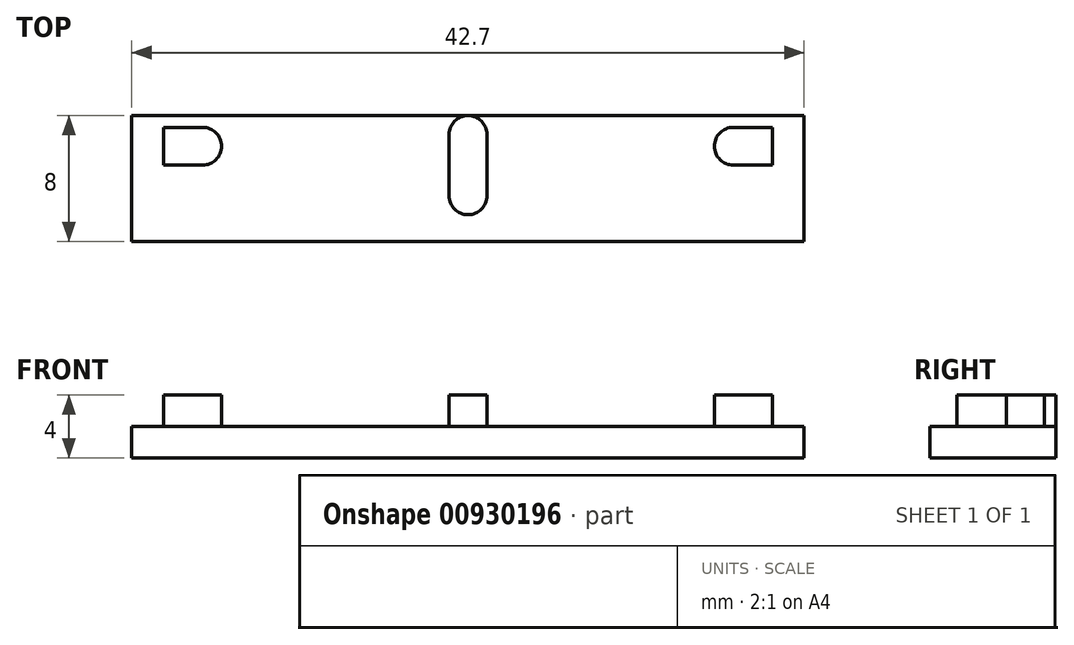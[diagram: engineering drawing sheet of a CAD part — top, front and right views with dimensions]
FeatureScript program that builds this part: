
annotation { "Feature Type Name" : "Feature", "Feature Type Description" : "" }
export const myFeature = defineFeature(function(context is Context, id is Id, definition is map)
    precondition{}
    {
        {
            var Q0;
            Q0=qCreatedBy(makeId("Top.planeOp"),FACE);
            var sketch = newSketch(context, id + "F0", { "sketchPlane" : qUnion([Q0])});
            skLineSegment(sketch, "E0.bottom", {"start": v(-19.35, 0) * mm, "end": v(19.35, 0) * mm});
            skLineSegment(sketch, "E0.top", {"start": v(-19.35, -12.3) * mm, "end": v(19.35, -12.3) * mm});
            skLineSegment(sketch, "E0.left", {"start": v(-19.35, 0) * mm, "end": v(-19.35, -1.15) * mm});
            skLineSegment(sketch, "E0.right", {"start": v(19.35, 0) * mm, "end": v(19.35, -1.15) * mm});
            skLineSegment(sketch, "E1.bottom", {"start": v(-19.85, 7) * mm, "end": v(19.85, 7) * mm});
            skLineSegment(sketch, "E1.top", {"start": v(-19.85, 0) * mm, "end": v(19.85, 0) * mm});
            skLineSegment(sketch, "E1.left", {"start": v(-19.85, 7) * mm, "end": v(-19.85, 0) * mm});
            skLineSegment(sketch, "E1.right", {"start": v(19.85, 7) * mm, "end": v(19.85, 0) * mm});
            skLineSegment(sketch, "E2", {"start": v(-19.35, -1.15) * mm, "end": v(-16.85, -1.15) * mm});
            skLineSegment(sketch, "E3", {"start": v(-19.35, -3.55) * mm, "end": v(-16.85, -3.55) * mm});
            skLineSegment(sketch, "E4", {"start": v(16.85, -3.55) * mm, "end": v(19.35, -3.55) * mm});
            skLineSegment(sketch, "E5", {"start": v(16.85, -1.15) * mm, "end": v(19.35, -1.15) * mm});
            skLineSegment(sketch, "E6.trimOffspring", {"start": v(-19.35, -3.55) * mm, "end": v(-19.35, -12.3) * mm});
            skLineSegment(sketch, "E7.trimOffspring", {"start": v(19.35, -3.55) * mm, "end": v(19.35, -12.3) * mm});
            skArc(sketch, "E8", {"start": v(-16.85, -3.55) * mm, "mid": v(-15.65, -2.35) * mm, "end": v(-16.85, -1.15) * mm});
            skArc(sketch, "E9", {"start": v(16.85, -1.15) * mm, "mid": v(15.65, -2.35) * mm, "end": v(16.85, -3.55) * mm});
            skLineSegment(sketch, "E10", {"start": v(-16.85, -2.35) * mm, "end": v(-15.65, -2.35) * mm, "construction": true});
            skLineSegment(sketch, "E11", {"start": v(-15.65, -2.35) * mm, "end": v(15.65, -2.35) * mm, "construction": true});
            skLineSegment(sketch, "E12", {"start": v(15.65, -2.35) * mm, "end": v(16.85, -2.35) * mm, "construction": true});
            skLineSegment(sketch, "E13", {"start": v(-1.2, -5.5) * mm, "end": v(-1.2, -1.6) * mm});
            skLineSegment(sketch, "E14", {"start": v(1.2, -5.5) * mm, "end": v(1.2, -1.6) * mm});
            skArc(sketch, "E15", {"start": v(1.2, -1.6) * mm, "mid": v(0, -0.4) * mm, "end": v(-1.2, -1.6) * mm});
            skArc(sketch, "E16", {"start": v(-1.2, -5.5) * mm, "mid": v(0, -6.7) * mm, "end": v(1.2, -5.5) * mm});
            skLineSegment(sketch, "E17", {"start": v(0, -1.6) * mm, "end": v(0, -5.5) * mm, "construction": true});
            skLineSegment(sketch, "E18", {"start": v(0, -1.6) * mm, "end": v(0, 0) * mm, "construction": true});
            skLineSegment(sketch, "E19", {"start": v(0, -0.4) * mm, "end": v(0, -6.7) * mm, "construction": true});
            skLineSegment(sketch, "E20", {"start": v(-19.35, -1.15) * mm, "end": v(-19.35, -3.55) * mm});
            skLineSegment(sketch, "E21", {"start": v(19.35, -1.15) * mm, "end": v(19.35, -3.55) * mm});
            skSolve(sketch);
        }
        {
            var Q0;
            Q0=makeQuery(id+"F0.imprint","IMPRINT",FACE,{"disambiguationData":[TD([[makeQuery(id+"F0.imprint","IMPRINT",EDGE,{"derivedFrom":sQuery(id+"F0.wireOp",EDGE,"E13")}),-1.0]])]});
            var Q1;
            Q1=makeQuery(id+"F0.imprint","IMPRINT",FACE,{"disambiguationData":[TD([[makeQuery(id+"F0.imprint","IMPRINT",EDGE,{"derivedFrom":sQuery(id+"F0.wireOp",EDGE,"E2")}),-1.0]])]});
            var Q2;
            Q2=makeQuery(id+"F0.imprint","IMPRINT",FACE,{"disambiguationData":[TD([[makeQuery(id+"F0.imprint","IMPRINT",EDGE,{"derivedFrom":sQuery(id+"F0.wireOp",EDGE,"E4")}),1.0]])]});
            extrude(context, id + "F1", {"entities" : qUnion([Q0, Q1, Q2]), "depth" : 2 * mm, "offsetDistance" : 25 * mm});
        }
        {
            var Q0;
            Q0=qCreatedBy(makeId("Top.planeOp"),FACE);
            var sketch = newSketch(context, id + "F2", { "sketchPlane" : qUnion([Q0])});
            skArc(sketch, "E22.0.0", {"start": v(-1.2, -5.5) * mm, "mid": v(0, -6.7) * mm, "end": v(1.2, -5.5) * mm, "construction": true});
            skLineSegment(sketch, "E22.0.1", {"start": v(1.2, -5.5) * mm, "end": v(1.2, -1.6) * mm, "construction": true});
            skArc(sketch, "E22.0.2", {"start": v(1.2, -1.6) * mm, "mid": v(0, -0.4) * mm, "end": v(-1.2, -1.6) * mm, "construction": true});
            skLineSegment(sketch, "E22.0.3", {"start": v(-1.2, -1.6) * mm, "end": v(-1.2, -5.5) * mm, "construction": true});
            skLineSegment(sketch, "E23.0.0", {"start": v(-19.35, -1.15) * mm, "end": v(-19.35, -3.55) * mm, "construction": true});
            skLineSegment(sketch, "E23.0.1", {"start": v(-19.35, -3.55) * mm, "end": v(-16.85, -3.55) * mm, "construction": true});
            skArc(sketch, "E23.0.2", {"start": v(-16.85, -3.55) * mm, "mid": v(-15.65, -2.35) * mm, "end": v(-16.85, -1.15) * mm, "construction": true});
            skLineSegment(sketch, "E23.0.3", {"start": v(-16.85, -1.15) * mm, "end": v(-19.35, -1.15) * mm, "construction": true});
            skLineSegment(sketch, "E24.bottom", {"start": v(21.35, -0.4) * mm, "end": v(-21.35, -0.4) * mm});
            skLineSegment(sketch, "E24.top", {"start": v(21.35, -8.4) * mm, "end": v(-21.35, -8.4) * mm});
            skLineSegment(sketch, "E24.left", {"start": v(21.35, -0.4) * mm, "end": v(21.35, -8.4) * mm});
            skLineSegment(sketch, "E24.right", {"start": v(-21.35, -0.4) * mm, "end": v(-21.35, -8.4) * mm});
            skPoint(sketch, "E25", {"position": v(0, -0.4) * mm});
            skSolve(sketch);
        }
        {
            var Q0;
            Q0=makeQuery(id+"F2.imprint","IMPRINT",FACE,{"disambiguationData":[TD([[makeQuery(id+"F2.imprint","IMPRINT",EDGE,{"derivedFrom":sQuery(id+"F2.wireOp",EDGE,"E24.bottom")}),1.0]])]});
            extrude(context, id + "F3", {"entities" : qUnion([Q0]), "operationType" : NewBodyOperationType.ADD, "oppositeDirection" : true, "depth" : 2 * mm, "offsetDistance" : 25 * mm});
        }
    });
